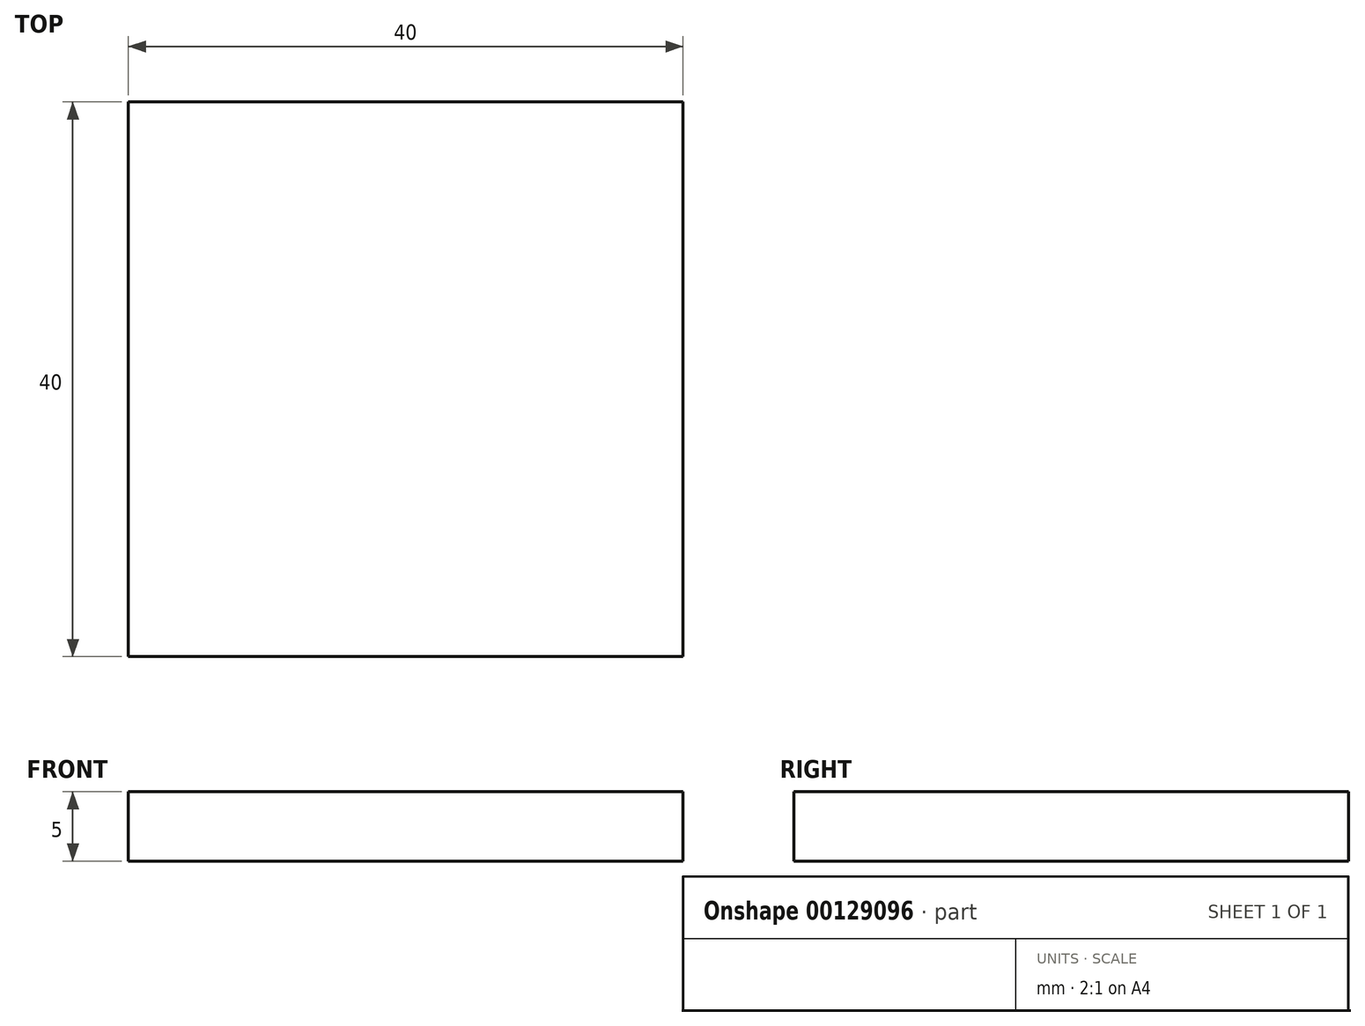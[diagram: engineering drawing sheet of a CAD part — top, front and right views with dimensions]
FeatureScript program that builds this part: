
annotation { "Feature Type Name" : "Feature", "Feature Type Description" : "" }
export const myFeature = defineFeature(function(context is Context, id is Id, definition is map)
    precondition{}
    {
        {
            var Q0;
            Q0=qCreatedBy(makeId("Top.planeOp"),FACE);
            var sketch = newSketch(context, id + "F0", { "sketchPlane" : qUnion([Q0])});
            skLineSegment(sketch, "E0.bottom", {"start": v(-11.07, 1.97) * mm, "end": v(28.93, 1.97) * mm});
            skLineSegment(sketch, "E0.top", {"start": v(-11.07, -38.03) * mm, "end": v(28.93, -38.03) * mm});
            skLineSegment(sketch, "E0.left", {"start": v(-11.07, 1.97) * mm, "end": v(-11.07, -38.03) * mm});
            skLineSegment(sketch, "E0.right", {"start": v(28.93, 1.97) * mm, "end": v(28.93, -38.03) * mm});
            skSolve(sketch);
        }
        {
            var Q0;
            Q0 = qSketchRegion(id + "F0", true);
            extrude(context, id + "F1", {"entities" : qUnion([Q0]), "depth" : 5 * mm});
        }
    });
